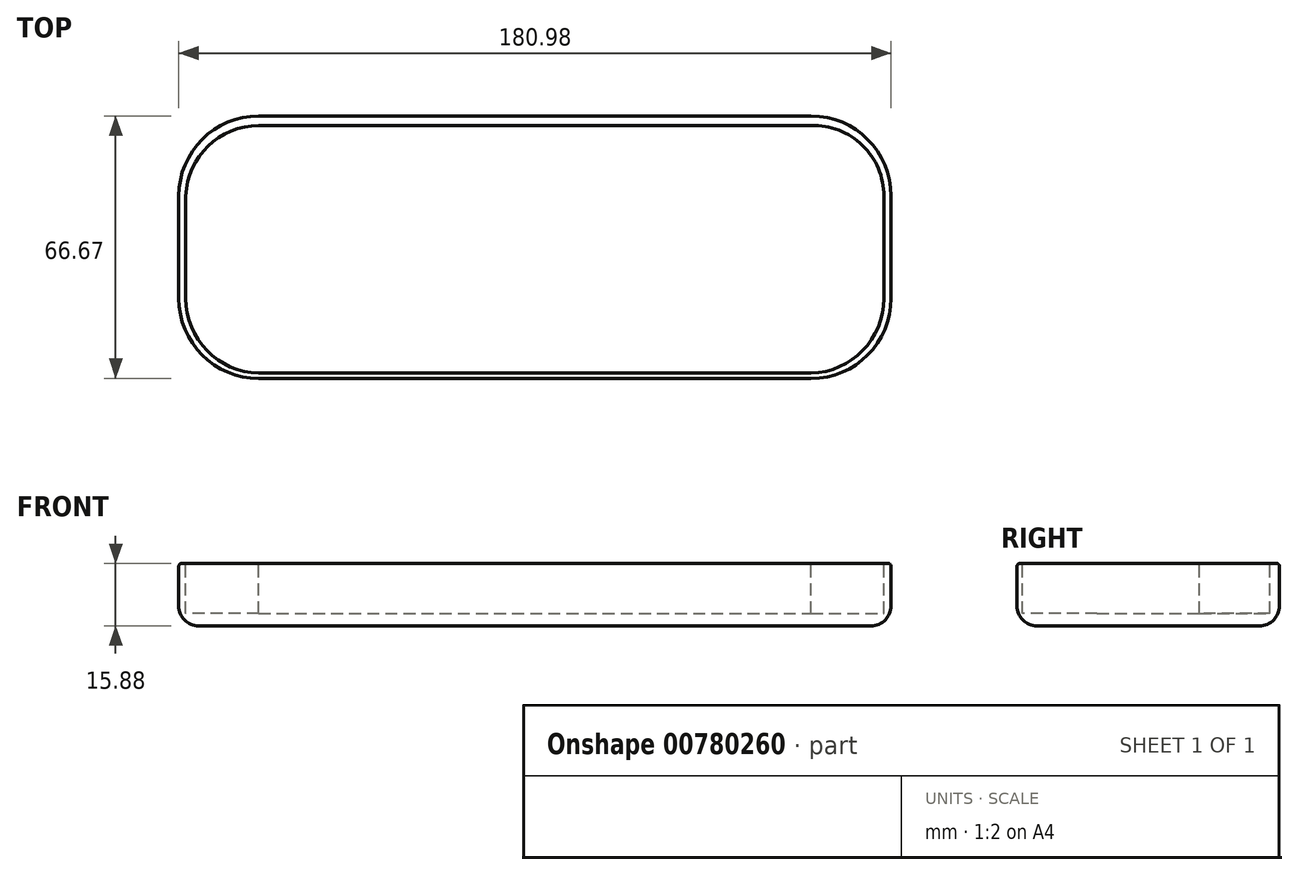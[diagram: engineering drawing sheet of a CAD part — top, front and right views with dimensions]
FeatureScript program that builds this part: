
annotation { "Feature Type Name" : "Feature", "Feature Type Description" : "" }
export const myFeature = defineFeature(function(context is Context, id is Id, definition is map)
    precondition{}
    {
        {
            var Q0;
            Q0=qCreatedBy(makeId("Top.planeOp"),FACE);
            var sketch = newSketch(context, id + "F0", { "sketchPlane" : qUnion([Q0])});
            skLineSegment(sketch, "E0.bottom", {"start": v(-74.66, 3.8) * mm, "end": v(106.32, 3.8) * mm});
            skLineSegment(sketch, "E0.top", {"start": v(-74.66, 70.48) * mm, "end": v(106.32, 70.48) * mm});
            skLineSegment(sketch, "E0.left", {"start": v(-74.66, 3.8) * mm, "end": v(-74.66, 70.48) * mm});
            skLineSegment(sketch, "E0.right", {"start": v(106.32, 3.8) * mm, "end": v(106.32, 70.48) * mm});
            skSolve(sketch);
        }
        {
            var Q0;
            Q0=qSketchRegion(id+"F0",true);
            extrude(context, id + "F1", {"entities" : qUnion([Q0]), "depth" : 15.88 * mm, "offsetDistance" : 25.4 * mm});
        }
        {
            var Q0;
            Q0=makeQuery(id+"F1.opExtrude","SWEPT_EDGE",EDGE,{"disambiguationData":[OSD([sQuery(id+"F0.wireOp",EDGE,"E0.top"),sQuery(id+"F0.wireOp",EDGE,"E0.right")])]});
            var Q1;
            Q1=makeQuery(id+"F1.opExtrude","SWEPT_EDGE",EDGE,{"disambiguationData":[OSD([sQuery(id+"F0.wireOp",EDGE,"E0.bottom"),sQuery(id+"F0.wireOp",EDGE,"E0.right")])]});
            var Q2;
            Q2=makeQuery(id+"F1.opExtrude","SWEPT_EDGE",EDGE,{"disambiguationData":[OSD([sQuery(id+"F0.wireOp",EDGE,"E0.top"),sQuery(id+"F0.wireOp",EDGE,"E0.left")])]});
            var Q3;
            Q3=makeQuery(id+"F1.opExtrude","SWEPT_EDGE",EDGE,{"disambiguationData":[OSD([sQuery(id+"F0.wireOp",EDGE,"E0.bottom"),sQuery(id+"F0.wireOp",EDGE,"E0.left")])]});
            fillet(context, id + "F2", {"entities" : qUnion([Q0, Q1, Q2, Q3]), "radius" : 20.32 * mm, "tangentPropagation" : true, "allowEdgeOverflow" : false});
        }
        {
            var Q0;
            Q0=makeQuery(id+"F1.opExtrude","CAP_EDGE",EDGE,{"disambiguationData":[OSD([sQuery(id+"F0.wireOp",EDGE,"E0.top")])],"isStart":true});
            fillet(context, id + "F3", {"entities" : qUnion([Q0]), "radius" : 5.08 * mm, "tangentPropagation" : true, "allowEdgeOverflow" : false});
        }
        {
            var Q0;
            Q0=makeQuery(id+"F1.opExtrude","CAP_FACE",FACE,{"disambiguationData":[OSD([sQuery(id+"F0.wireOp",EDGE,"E0.bottom"),sQuery(id+"F0.wireOp",EDGE,"E0.top"),sQuery(id+"F0.wireOp",EDGE,"E0.left"),sQuery(id+"F0.wireOp",EDGE,"E0.right")])],"isStart":false});
            var sketch = newSketch(context, id + "F4", { "sketchPlane" : qUnion([Q0])});
            skLineSegment(sketch, "E1", {"start": v(-54.34, 68.03) * mm, "end": v(86, 68.03) * mm});
            skLineSegment(sketch, "E2", {"start": v(86, 68.03) * mm, "end": v(104.5, 50.16) * mm});
            skLineSegment(sketch, "E3", {"start": v(104.5, 50.16) * mm, "end": v(104.5, 24.13) * mm});
            skLineSegment(sketch, "E4", {"start": v(104.5, 24.13) * mm, "end": v(86, 5.14) * mm});
            skLineSegment(sketch, "E5", {"start": v(86, 5.14) * mm, "end": v(-54.34, 5.14) * mm});
            skLineSegment(sketch, "E6", {"start": v(-54.34, 5.14) * mm, "end": v(-72.85, 24.13) * mm});
            skLineSegment(sketch, "E7", {"start": v(-72.85, 24.13) * mm, "end": v(-72.85, 50.16) * mm});
            skLineSegment(sketch, "E8", {"start": v(-72.85, 50.16) * mm, "end": v(-54.34, 68.03) * mm});
            skSolve(sketch);
        }
        {
            var Q0;
            Q0=qSketchRegion(id+"F4",true);
            extrude(context, id + "F5", {"entities" : qUnion([Q0]), "operationType" : NewBodyOperationType.REMOVE, "oppositeDirection" : true, "depth" : 12.7 * mm, "offsetDistance" : 25.4 * mm});
        }
        {
            var Q0;
            Q0=makeQuery(id+"F1.opExtrude","CAP_FACE",FACE,{"disambiguationData":[OSD([sQuery(id+"F0.wireOp",EDGE,"E0.bottom"),sQuery(id+"F0.wireOp",EDGE,"E0.top"),sQuery(id+"F0.wireOp",EDGE,"E0.left"),sQuery(id+"F0.wireOp",EDGE,"E0.right")])],"isStart":false});
            var sketch = newSketch(context, id + "F6", { "sketchPlane" : qUnion([Q0])});
            skArc(sketch, "E9", {"start": v(86, 5.14) * mm, "mid": v(99.1, 10.88) * mm, "end": v(104.5, 24.13) * mm});
            skSolve(sketch);
        }
        {
            var Q0;
            Q0=makeQuery(id+"F6.imprint","IMPRINT",FACE,{"disambiguationData":[TD([[makeQuery(id+"F6.imprint","IMPRINT",EDGE,{"derivedFrom":sQuery(id+"F6.wireOp",EDGE,"E9")}),1.0]])]});
            extrude(context, id + "F7", {"entities" : qUnion([Q0]), "operationType" : NewBodyOperationType.REMOVE, "oppositeDirection" : true, "depth" : 12.7 * mm, "offsetDistance" : 25.4 * mm});
        }
        {
            var Q0;
            Q0=makeQuery(id+"F1.opExtrude","CAP_FACE",FACE,{"disambiguationData":[OSD([sQuery(id+"F0.wireOp",EDGE,"E0.bottom"),sQuery(id+"F0.wireOp",EDGE,"E0.top"),sQuery(id+"F0.wireOp",EDGE,"E0.left"),sQuery(id+"F0.wireOp",EDGE,"E0.right")])],"isStart":false});
            var sketch = newSketch(context, id + "F8", { "sketchPlane" : qUnion([Q0])});
            skArc(sketch, "E10", {"start": v(-72.85, 24.13) * mm, "mid": v(-67.46, 10.87) * mm, "end": v(-54.34, 5.14) * mm});
            skSolve(sketch);
        }
        {
            var Q0;
            Q0=makeQuery(id+"F8.imprint","IMPRINT",FACE,{"disambiguationData":[TD([[makeQuery(id+"F8.imprint","IMPRINT",EDGE,{"derivedFrom":sQuery(id+"F8.wireOp",EDGE,"E10")}),1.0]])]});
            extrude(context, id + "F9", {"entities" : qUnion([Q0]), "operationType" : NewBodyOperationType.REMOVE, "oppositeDirection" : true, "depth" : 12.7 * mm, "offsetDistance" : 25.4 * mm});
        }
        {
            var Q0;
            Q0=makeQuery(id+"F1.opExtrude","CAP_FACE",FACE,{"disambiguationData":[OSD([sQuery(id+"F0.wireOp",EDGE,"E0.bottom"),sQuery(id+"F0.wireOp",EDGE,"E0.top"),sQuery(id+"F0.wireOp",EDGE,"E0.left"),sQuery(id+"F0.wireOp",EDGE,"E0.right")])],"isStart":false});
            var sketch = newSketch(context, id + "F10", { "sketchPlane" : qUnion([Q0])});
            skArc(sketch, "E11", {"start": v(-54.34, 68.03) * mm, "mid": v(-67.2, 62.84) * mm, "end": v(-72.85, 50.16) * mm});
            skSolve(sketch);
        }
        {
            var Q0;
            Q0=makeQuery(id+"F10.imprint","IMPRINT",FACE,{"disambiguationData":[TD([[makeQuery(id+"F10.imprint","IMPRINT",EDGE,{"derivedFrom":sQuery(id+"F10.wireOp",EDGE,"E11")}),1.0]])]});
            extrude(context, id + "F11", {"entities" : qUnion([Q0]), "operationType" : NewBodyOperationType.REMOVE, "oppositeDirection" : true, "depth" : 12.7 * mm, "offsetDistance" : 25.4 * mm});
        }
        {
            var Q0;
            Q0=makeQuery(id+"F1.opExtrude","CAP_FACE",FACE,{"disambiguationData":[OSD([sQuery(id+"F0.wireOp",EDGE,"E0.bottom"),sQuery(id+"F0.wireOp",EDGE,"E0.top"),sQuery(id+"F0.wireOp",EDGE,"E0.left"),sQuery(id+"F0.wireOp",EDGE,"E0.right")])],"isStart":false});
            var sketch = newSketch(context, id + "F12", { "sketchPlane" : qUnion([Q0])});
            skArc(sketch, "E12", {"start": v(104.5, 50.16) * mm, "mid": v(99.04, 63.02) * mm, "end": v(86, 68.03) * mm});
            skSolve(sketch);
        }
        {
            var Q0;
            Q0=makeQuery(id+"F12.imprint","IMPRINT",FACE,{"disambiguationData":[TD([[makeQuery(id+"F12.imprint","IMPRINT",EDGE,{"derivedFrom":sQuery(id+"F12.wireOp",EDGE,"E12")}),1.0]])]});
            extrude(context, id + "F13", {"entities" : qUnion([Q0]), "operationType" : NewBodyOperationType.REMOVE, "oppositeDirection" : true, "depth" : 12.7 * mm, "offsetDistance" : 25.4 * mm});
        }
        {
            var Q0;
            Q0=makeQuery(id+"F5.boolean.opBoolean","COPY",EDGE,{"derivedFrom":makeQuery(id+"F5.opExtrude","CAP_EDGE",EDGE,{"disambiguationData":[OSD([sQuery(id+"F4.wireOp",EDGE,"E5")])],"isStart":true})});
            var Q1;
            Q1=makeQuery(id+"F1.opExtrude","CAP_EDGE",EDGE,{"disambiguationData":[OSD([sQuery(id+"F0.wireOp",EDGE,"E0.bottom")])],"isStart":false});
            var Q2;
            Q2=makeQuery(id+"F9.boolean.opBoolean","COPY",EDGE,{"derivedFrom":makeQuery(id+"F9.opExtrude","CAP_EDGE",EDGE,{"disambiguationData":[OSD([sQuery(id+"F8.wireOp",EDGE,"E10")])],"isStart":true})});
            var Q3;
            {var subQ0=sQuery(id+"F0.wireOp",EDGE,"E0.left");var subQ1=sQuery(id+"F0.wireOp",EDGE,"E0.bottom");Q3=makeQuery(id+"F2.opFillet","BLEND_EDGE",EDGE,{"blendedFrom":[makeQuery(id+"F1.opExtrude","SWEPT_EDGE",EDGE,{"disambiguationData":[OSD([subQ1,subQ0])]}),makeQuery(id+"F1.opExtrude","CAP_FACE",FACE,{"disambiguationData":[OSD([subQ1,sQuery(id+"F0.wireOp",EDGE,"E0.top"),subQ0,sQuery(id+"F0.wireOp",EDGE,"E0.right")])],"isStart":false})],"blendedInto":[makeQuery(id+"F1.opExtrude","CAP_FACE",FACE,{"disambiguationData":[OSD([subQ1,sQuery(id+"F0.wireOp",EDGE,"E0.top"),subQ0,sQuery(id+"F0.wireOp",EDGE,"E0.right")])],"isStart":false})]});}
            var Q4;
            Q4=makeQuery(id+"F5.boolean.opBoolean","COPY",EDGE,{"derivedFrom":makeQuery(id+"F5.opExtrude","CAP_EDGE",EDGE,{"disambiguationData":[OSD([sQuery(id+"F4.wireOp",EDGE,"E7")])],"isStart":true})});
            var Q5;
            Q5=makeQuery(id+"F1.opExtrude","CAP_EDGE",EDGE,{"disambiguationData":[OSD([sQuery(id+"F0.wireOp",EDGE,"E0.left")])],"isStart":false});
            var Q6;
            {var subQ0=sQuery(id+"F0.wireOp",EDGE,"E0.left");var subQ1=sQuery(id+"F0.wireOp",EDGE,"E0.top");Q6=makeQuery(id+"F2.opFillet","BLEND_EDGE",EDGE,{"blendedFrom":[makeQuery(id+"F1.opExtrude","SWEPT_EDGE",EDGE,{"disambiguationData":[OSD([subQ1,subQ0])]}),makeQuery(id+"F1.opExtrude","CAP_FACE",FACE,{"disambiguationData":[OSD([sQuery(id+"F0.wireOp",EDGE,"E0.bottom"),subQ1,subQ0,sQuery(id+"F0.wireOp",EDGE,"E0.right")])],"isStart":false})],"blendedInto":[makeQuery(id+"F1.opExtrude","CAP_FACE",FACE,{"disambiguationData":[OSD([sQuery(id+"F0.wireOp",EDGE,"E0.bottom"),subQ1,subQ0,sQuery(id+"F0.wireOp",EDGE,"E0.right")])],"isStart":false})]});}
            var Q7;
            Q7=makeQuery(id+"F11.boolean.opBoolean","COPY",EDGE,{"derivedFrom":makeQuery(id+"F11.opExtrude","CAP_EDGE",EDGE,{"disambiguationData":[OSD([sQuery(id+"F10.wireOp",EDGE,"E11")])],"isStart":true})});
            var Q8;
            Q8=makeQuery(id+"F1.opExtrude","CAP_EDGE",EDGE,{"disambiguationData":[OSD([sQuery(id+"F0.wireOp",EDGE,"E0.top")])],"isStart":false});
            var Q9;
            Q9=makeQuery(id+"F5.boolean.opBoolean","COPY",EDGE,{"derivedFrom":makeQuery(id+"F5.opExtrude","CAP_EDGE",EDGE,{"disambiguationData":[OSD([sQuery(id+"F4.wireOp",EDGE,"E1")])],"isStart":true})});
            var Q10;
            Q10=makeQuery(id+"F13.boolean.opBoolean","COPY",EDGE,{"derivedFrom":makeQuery(id+"F13.opExtrude","CAP_EDGE",EDGE,{"disambiguationData":[OSD([sQuery(id+"F12.wireOp",EDGE,"E12")])],"isStart":true})});
            var Q11;
            {var subQ0=sQuery(id+"F0.wireOp",EDGE,"E0.right");var subQ1=sQuery(id+"F0.wireOp",EDGE,"E0.top");Q11=makeQuery(id+"F2.opFillet","BLEND_EDGE",EDGE,{"blendedFrom":[makeQuery(id+"F1.opExtrude","SWEPT_EDGE",EDGE,{"disambiguationData":[OSD([subQ1,subQ0])]}),makeQuery(id+"F1.opExtrude","CAP_FACE",FACE,{"disambiguationData":[OSD([sQuery(id+"F0.wireOp",EDGE,"E0.bottom"),subQ1,sQuery(id+"F0.wireOp",EDGE,"E0.left"),subQ0])],"isStart":false})],"blendedInto":[makeQuery(id+"F1.opExtrude","CAP_FACE",FACE,{"disambiguationData":[OSD([sQuery(id+"F0.wireOp",EDGE,"E0.bottom"),subQ1,sQuery(id+"F0.wireOp",EDGE,"E0.left"),subQ0])],"isStart":false})]});}
            var Q12;
            Q12=makeQuery(id+"F5.boolean.opBoolean","COPY",EDGE,{"derivedFrom":makeQuery(id+"F5.opExtrude","CAP_EDGE",EDGE,{"disambiguationData":[OSD([sQuery(id+"F4.wireOp",EDGE,"E3")])],"isStart":true})});
            var Q13;
            Q13=makeQuery(id+"F1.opExtrude","CAP_EDGE",EDGE,{"disambiguationData":[OSD([sQuery(id+"F0.wireOp",EDGE,"E0.right")])],"isStart":false});
            var Q14;
            Q14=makeQuery(id+"F7.boolean.opBoolean","COPY",EDGE,{"derivedFrom":makeQuery(id+"F7.opExtrude","CAP_EDGE",EDGE,{"disambiguationData":[OSD([sQuery(id+"F6.wireOp",EDGE,"E9")])],"isStart":true})});
            var Q15;
            {var subQ0=sQuery(id+"F0.wireOp",EDGE,"E0.right");var subQ1=sQuery(id+"F0.wireOp",EDGE,"E0.bottom");Q15=makeQuery(id+"F2.opFillet","BLEND_EDGE",EDGE,{"blendedFrom":[makeQuery(id+"F1.opExtrude","SWEPT_EDGE",EDGE,{"disambiguationData":[OSD([subQ1,subQ0])]}),makeQuery(id+"F1.opExtrude","CAP_FACE",FACE,{"disambiguationData":[OSD([subQ1,sQuery(id+"F0.wireOp",EDGE,"E0.top"),sQuery(id+"F0.wireOp",EDGE,"E0.left"),subQ0])],"isStart":false})],"blendedInto":[makeQuery(id+"F1.opExtrude","CAP_FACE",FACE,{"disambiguationData":[OSD([subQ1,sQuery(id+"F0.wireOp",EDGE,"E0.top"),sQuery(id+"F0.wireOp",EDGE,"E0.left"),subQ0])],"isStart":false})]});}
            fillet(context, id + "F14", {"entities" : qUnion([Q0, Q1, Q2, Q3, Q4, Q5, Q6, Q7, Q8, Q9, Q10, Q11, Q12, Q13, Q14, Q15]), "radius" : 0.76 * mm, "tangentPropagation" : true, "allowEdgeOverflow" : false});
        }
    });
